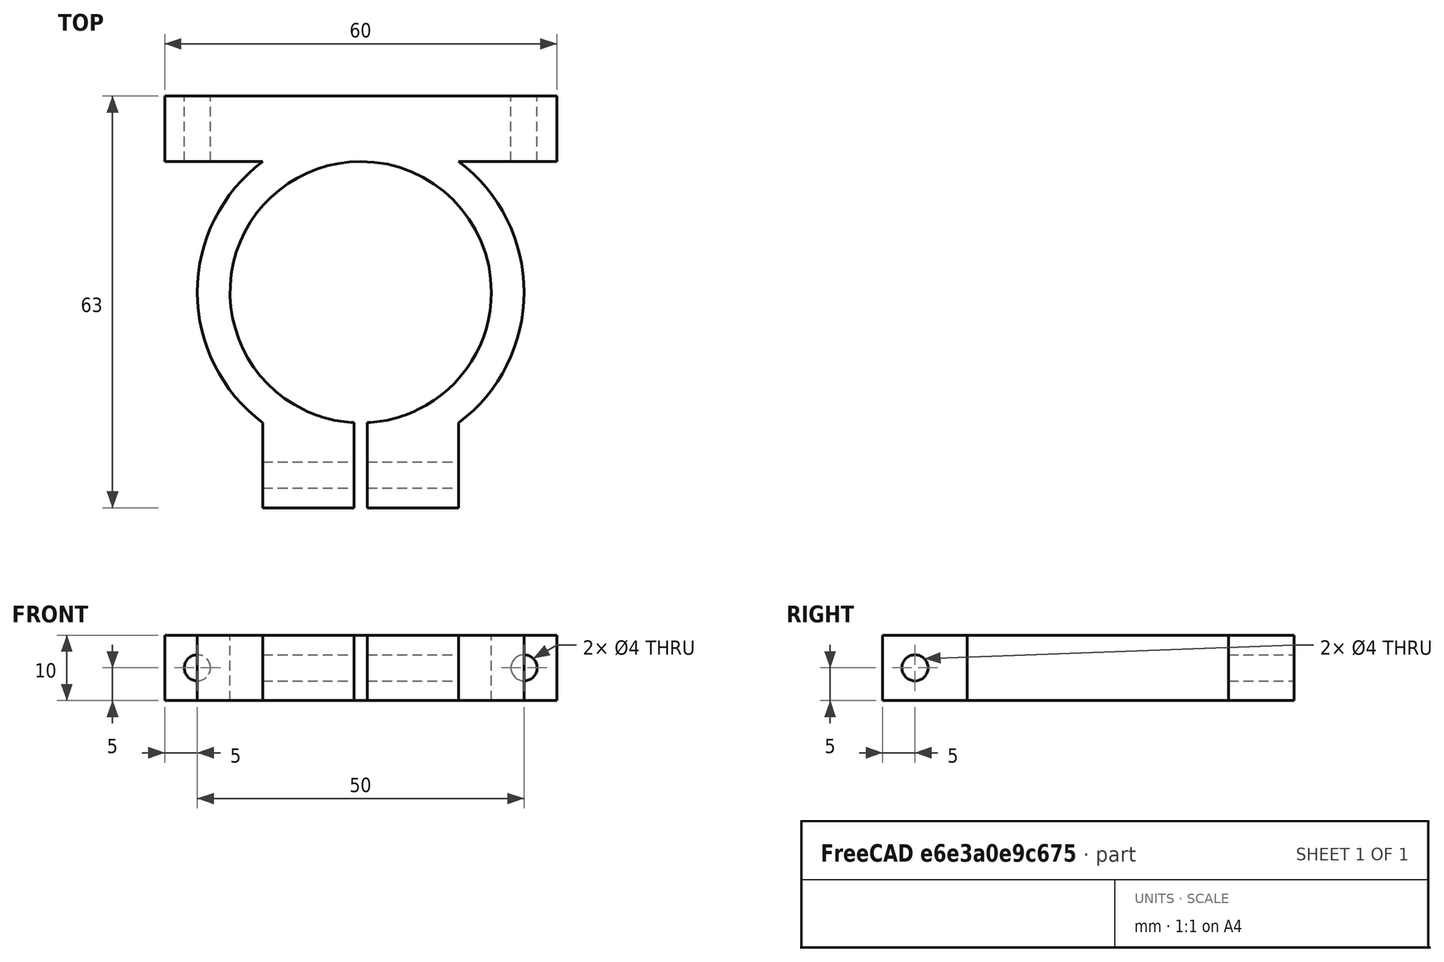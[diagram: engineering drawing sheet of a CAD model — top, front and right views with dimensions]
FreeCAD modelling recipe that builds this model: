
FCSTD DOCUMENT  (FreeCAD 0.18R16110 (Git))
Label: EncoderAttachment
License: All rights reserved
LicenseURL: http://en.wikipedia.org/wiki/All_rights_reserved
objects: Part::Cylinder×5, Part::Box×3, Part::MultiFuse×2, Part::Cut×1
note: 11 computed .brp shape members not serialized (recipe doc carries the construction recipe); baked Part::Feature solids carry a one-line shape summary decoded from their .brp

FEATURE [Part::Cylinder] Cylinder
  Angle = 360
  AttacherType = Attacher::AttachEngine3D
  Height = 10
  Placement = pos=(0,0,-5) rot=(0,0,1;0rad)
  Radius = 25
FEATURE [Part::Cylinder] Cylinder001
  Angle = 360
  AttacherType = Attacher::AttachEngine3D
  Height = 10
  Placement = pos=(0,0,-5) rot=(0,0,1;0rad)
  Radius = 20
FEATURE [Part::Box] Box  label="Cube"
  AttacherType = Attacher::AttachEngine3D
  Height = 10
  Length = 60
  Placement = pos=(-30,20,-5) rot=(0,0,1;0rad)
  Width = 10
FEATURE [Part::Cylinder] Cylinder002
  Angle = 360
  AttacherType = Attacher::AttachEngine3D
  Height = 10
  Placement = pos=(25,20,-4e-15) rot=(-1,0,0;1.5708rad)
  Radius = 2
FEATURE [Part::Cylinder] Cylinder003
  Angle = 360
  AttacherType = Attacher::AttachEngine3D
  Height = 10
  Placement = pos=(-25,20,-4e-15) rot=(-1,0,0;1.5708rad)
  Radius = 2
FEATURE [Part::Box] Box001  label="Cube001"
  AttacherType = Attacher::AttachEngine3D
  Height = 10
  Length = 30
  Placement = pos=(-15,-33,-5) rot=(0,0,1;0rad)
  Width = 15
FEATURE [Part::MultiFuse] Fusion  label="Positive Fusion"
  Shapes = -> [Cylinder,Box,Box001]
FEATURE [Part::Cylinder] Cylinder004
  Angle = 360
  AttacherType = Attacher::AttachEngine3D
  Height = 30
  Placement = pos=(-15,-28,-3.3e-15) rot=(0,1,0;1.5708rad)
  Radius = 2
FEATURE [Part::Box] Box002  label="Cube002"
  AttacherType = Attacher::AttachEngine3D
  Height = 10
  Length = 2
  Placement = pos=(-1,-33,-5) rot=(0,0,1;0rad)
  Width = 15
FEATURE [Part::MultiFuse] Fusion001  label="Negative Fusion"
  Shapes = -> [Cylinder003,Cylinder002,Cylinder001,Cylinder004,Box002]
FEATURE [Part::Cut] Cut
  Base = -> Fusion
  Tool = -> Fusion001
